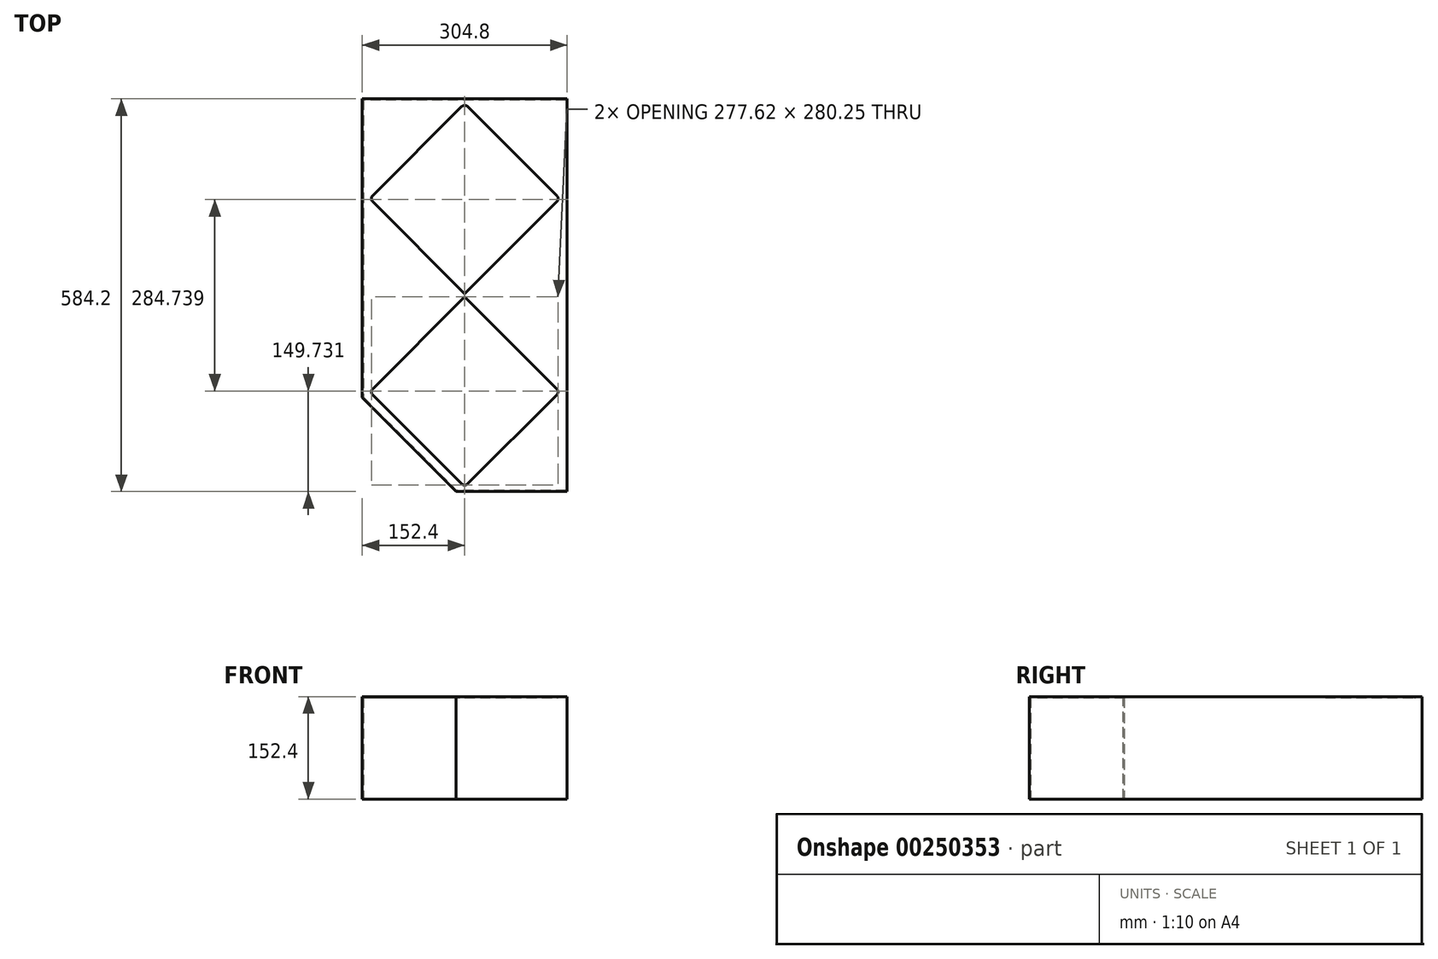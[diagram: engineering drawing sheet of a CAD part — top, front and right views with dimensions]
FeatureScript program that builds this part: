
annotation { "Feature Type Name" : "Feature", "Feature Type Description" : "" }
export const myFeature = defineFeature(function(context is Context, id is Id, definition is map)
    precondition{}
    {
        {
            var Q0;
            Q0=qCreatedBy(makeId("Top.planeOp"),FACE);
            var sketch = newSketch(context, id + "F0", { "sketchPlane" : qUnion([Q0])});
            skLineSegment(sketch, "E0.bottom", {"start": v(152.4, 292.1) * mm, "end": v(-152.4, 292.1) * mm});
            skLineSegment(sketch, "E0.top", {"start": v(152.4, -292.1) * mm, "end": v(-152.4, -292.1) * mm});
            skLineSegment(sketch, "E0.left", {"start": v(152.4, 292.1) * mm, "end": v(152.4, -292.1) * mm});
            skLineSegment(sketch, "E0.right", {"start": v(-152.4, 292.1) * mm, "end": v(-152.4, -292.1) * mm});
            skPoint(sketch, "E0.middle", {"position": v(0, 0) * mm});
            skSolve(sketch);
        }
        {
            var Q0;
            Q0=qSketchRegion(id+"F0",true);
            extrude(context, id + "F1", {"entities" : qUnion([Q0]), "depth" : 152.4 * mm});
        }
        {
            var Q0;
            Q0=makeQuery(id+"F1.opExtrude","CAP_FACE",FACE,{"disambiguationData":[OSD([sQuery(id+"F0.wireOp",EDGE,"E0.bottom"),sQuery(id+"F0.wireOp",EDGE,"E0.top"),sQuery(id+"F0.wireOp",EDGE,"E0.left"),sQuery(id+"F0.wireOp",EDGE,"E0.right")])],"isStart":true});
            shell(context, id + "F2", {"entities" : qUnion([Q0]), "thickness" : 1.59 * mm});
        }
        {
            var Q0;
            Q0=makeQuery(id+"F1.opExtrude","CAP_FACE",FACE,{"disambiguationData":[OSD([sQuery(id+"F0.wireOp",EDGE,"E0.bottom"),sQuery(id+"F0.wireOp",EDGE,"E0.top"),sQuery(id+"F0.wireOp",EDGE,"E0.left"),sQuery(id+"F0.wireOp",EDGE,"E0.right")])],"isStart":false});
            var sketch = newSketch(context, id + "F3", { "sketchPlane" : qUnion([Q0])});
            skLineSegment(sketch, "E1", {"start": v(0, 292.1) * mm, "end": v(0, -292.1) * mm});
            skLineSegment(sketch, "E2", {"start": v(0, -292.1) * mm, "end": v(0, 0) * mm});
            skLineSegment(sketch, "E3", {"start": v(0, 0) * mm, "end": v(-152.4, 0) * mm});
            skLineSegment(sketch, "E4", {"start": v(-152.4, 0) * mm, "end": v(152.4, 0) * mm});
            skLineSegment(sketch, "E5", {"start": v(0, 0) * mm, "end": v(0, 2.25) * mm});
            skLineSegment(sketch, "E6", {"start": v(0, 2.25) * mm, "end": v(0, 0) * mm});
            skLineSegment(sketch, "E7", {"start": v(0, 0) * mm, "end": v(0, -2.25) * mm});
            skLineSegment(sketch, "E8", {"start": v(0, 2.25) * mm, "end": v(136.95, 139.2) * mm});
            skLineSegment(sketch, "E9", {"start": v(136.95, 148.17) * mm, "end": v(4.5, 280.63) * mm});
            skLineSegment(sketch, "E10", {"start": v(-4.5, 280.63) * mm, "end": v(-136.95, 148.17) * mm});
            skLineSegment(sketch, "E11", {"start": v(-136.95, 139.2) * mm, "end": v(0, 2.25) * mm});
            skLineSegment(sketch, "E12.MirrorCS", {"start": v(0, -2.25) * mm, "end": v(136.95, -139.2) * mm});
            skLineSegment(sketch, "E13.MirrorCS", {"start": v(136.95, -148.17) * mm, "end": v(4.5, -280.63) * mm});
            skLineSegment(sketch, "E14.MirrorCS", {"start": v(-4.5, -280.63) * mm, "end": v(-136.95, -148.17) * mm});
            skLineSegment(sketch, "E15.MirrorCS", {"start": v(-136.95, -139.2) * mm, "end": v(0, -2.25) * mm});
            skPoint(sketch, "E16.visualSharp", {"position": v(-141.44, 143.68) * mm});
            skArc(sketch, "E16.filletArc", {"start": v(-136.95, 148.17) * mm, "mid": v(-138.8, 143.68) * mm, "end": v(-136.95, 139.2) * mm});
            skPoint(sketch, "E17.visualSharp", {"position": v(141.44, 143.68) * mm});
            skArc(sketch, "E17.filletArc", {"start": v(136.95, 139.2) * mm, "mid": v(138.8, 143.68) * mm, "end": v(136.95, 148.17) * mm});
            skPoint(sketch, "E18.visualSharp", {"position": v(0, 285.12) * mm});
            skArc(sketch, "E18.filletArc", {"start": v(4.5, 280.63) * mm, "mid": v(0, 282.5) * mm, "end": v(-4.5, 280.63) * mm});
            skPoint(sketch, "E19.visualSharp", {"position": v(-141.44, -143.68) * mm});
            skArc(sketch, "E19.filletArc", {"start": v(-136.95, -139.2) * mm, "mid": v(-138.8, -143.68) * mm, "end": v(-136.95, -148.17) * mm});
            skPoint(sketch, "E20.visualSharp", {"position": v(141.44, -143.68) * mm});
            skArc(sketch, "E20.filletArc", {"start": v(136.95, -148.17) * mm, "mid": v(138.8, -143.68) * mm, "end": v(136.95, -139.2) * mm});
            skPoint(sketch, "E21.visualSharp", {"position": v(0, -285.12) * mm});
            skArc(sketch, "E21.filletArc", {"start": v(-4.5, -280.63) * mm, "mid": v(0, -282.5) * mm, "end": v(4.5, -280.63) * mm});
            skSolve(sketch);
        }
        {
            var Q0;
            Q0=qSketchRegion(id+"F3",true);
            extrude(context, id + "F4", {"entities" : qUnion([Q0]), "operationType" : NewBodyOperationType.REMOVE, "oppositeDirection" : true, "depth" : 25.4 * mm});
        }
        {
            var Q0;
            Q0=makeQuery(id+"F1.opExtrude","CAP_FACE",FACE,{"disambiguationData":[OSD([sQuery(id+"F0.wireOp",EDGE,"E0.bottom"),sQuery(id+"F0.wireOp",EDGE,"E0.top"),sQuery(id+"F0.wireOp",EDGE,"E0.left"),sQuery(id+"F0.wireOp",EDGE,"E0.right")])],"isStart":false});
            var sketch = newSketch(context, id + "F5", { "sketchPlane" : qUnion([Q0])});
            skLineSegment(sketch, "E22", {"start": v(-152.4, -152.4) * mm, "end": v(-12.7, -292.1) * mm});
            skSolve(sketch);
        }
        {
            var Q0;
            Q0 = qSketchRegion(id + "F5", true);
            var Q1;
            {var subQ0=sQuery(id+"F5.wireOp",EDGE,"E22");Q1=makeQuery(id+"F5.imprint","IMPRINT",FACE,{"disambiguationData":[TD([[makeQuery(id+"F5.imprint","IMPRINT",EDGE,{"derivedFrom":subQ0}),-1.0]])]});}
            extrude(context, id + "F6", {"entities" : qUnion([Q0, Q1]), "operationType" : NewBodyOperationType.REMOVE, "endBound" : BoundingType.THROUGH_ALL, "oppositeDirection" : true, "depth" : 25.4 * mm});
        }
        {
            var Q0;
            Q0=makeQuery(id+"F6.boolean.opBoolean","COPY",FACE,{"derivedFrom":makeQuery(id+"F6.opExtrude","SWEPT_FACE",FACE,{"disambiguationData":[OSD([sQuery(id+"F5.wireOp",EDGE,"E22")])]})});
            var sketch = newSketch(context, id + "F7", { "sketchPlane" : qUnion([Q0])});
            skLineSegment(sketch, "E23.bottom", {"start": v(0, 152.4) * mm, "end": v(197.57, 152.4) * mm});
            skLineSegment(sketch, "E23.top", {"start": v(0, 0) * mm, "end": v(197.57, 0) * mm});
            skLineSegment(sketch, "E23.left", {"start": v(0, 152.4) * mm, "end": v(0, 0) * mm});
            skLineSegment(sketch, "E23.right", {"start": v(197.57, 152.4) * mm, "end": v(197.57, 0) * mm});
            skSolve(sketch);
        }
        {
            var Q0;
            Q0 = qSketchRegion(id + "F7", true);
            extrude(context, id + "F8", {"entities" : qUnion([Q0]), "operationType" : NewBodyOperationType.ADD, "oppositeDirection" : true, "depth" : 1.59 * mm});
        }
    });
